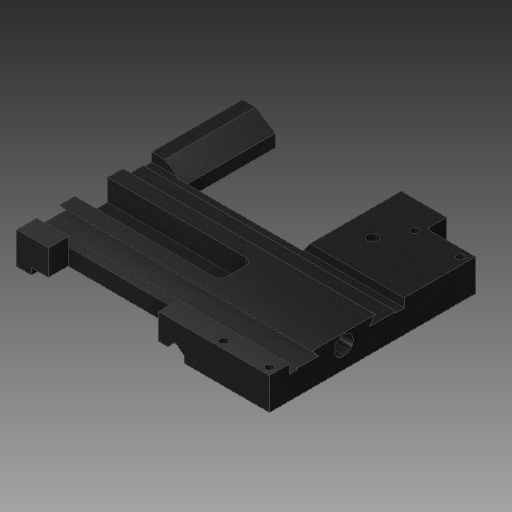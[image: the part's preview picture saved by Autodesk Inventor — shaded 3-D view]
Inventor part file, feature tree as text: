
AUTODESK INVENTOR PART (.ipt)
format: ipt  version: 2018 (Build 220112000, 112)  size: 340,480 bytes
history: native  units: in
note: dims shown in document units (in); Inventor stores cm internally (conversion verified against a paired STEP export)
features: extrude x14, sketch x9
ambient origin geometry x8: Origin, YZ Plane, XZ Plane, XY Plane, X Axis, Y Axis, Z Axis, Center Point
bodies: Solid1 (feature_tree)
feature tree (23):
  extrude  "Extrusion1"  Depth=13.5039in
  extrude  "Extrusion2"  Depth=1.9094in TaperAngle=0.0deg
  extrude  "Extrusion3"  Depth=1.378in
  extrude  "Extrusion4"  Depth=0.8933in
  extrude  "Extrusion8"  Depth=0.0787in
  extrude  "Extrusion19"  Depth=1.1811in
  extrude  "Extrusion21"  Depth=0.1181in
  extrude  "Extrusion22"  Depth=0.3937in
  extrude  "Extrusion23"  Depth=6.5748in
  extrude  "Extrusion24"  Depth=6.5748in
  extrude  "Extrusion25"  Depth=6.5748in
  extrude  "Extrusion26"  Depth=6.5748in
  extrude  "Extrusion27"  TaperAngle=0.0deg  [1 undecoded]
  extrude  "Extrusion28"  Depth=0.0787in TaperAngle=0.0deg
  sketch  "Sketch1"  dims[d0=15.1181in d1=13.5039in]
  sketch  "Sketch12"  dims[d2=1.9094in d3=0.0in d12=1.9094in d13=0.0in]
  sketch  "Sketch28"  dims[d23=1.378in d27=3.7795in]
  sketch  "Sketch32"  dims[d29=1.7323in d32=0.8933in]
  sketch  "Sketch36"  dims[d35=1.9094in d36=0.0in d37=0.0787in]
  sketch  "Sketch38"  dims[d38=0.5118in d43=1.1811in]
  sketch  "Sketch40"  dims[d44=1.9094in d45=0.0in d46=0.1181in]
  sketch  "Sketch41"  dims[d52=0.3436in d72=0.3937in]
  sketch  "Sketch42"  dims[d73=1.2992in d74=0.0in d146=0.4567in d149=0.4567in d152=0.4567in d155=0.4567in d156=0.0in d157=0.0in d161=0.0787in d162=0.0in d168=0.6299in d169=0.3937in d170=0.0in d209=0.6299in d210=45.0deg d211=0.1811in d214=0.5197in d215=45.0deg d216=0.4724in d224=0.8661in d225=0.3937in d227=0.3937in d228=0.0in d229=0.5512in d232=0.748in d233=5.5118in d234=0.0in d235=5.5118in d236=0.0in d240=0.5197in d242=0.1811in d243=0.6299in d245=5.5118in d246=0.0in d247=0.6693in d248=0.3937in d249=0.0in d250=1.1417in d251=2.2441in d252=0.0in d255=1.8898in d256=6.5748in]
note: 1 required parameter value undecoded (feature->parameter linkage not recoverable at this tier; creation-order binding heuristic only, values carry confidence <= 0.55)
